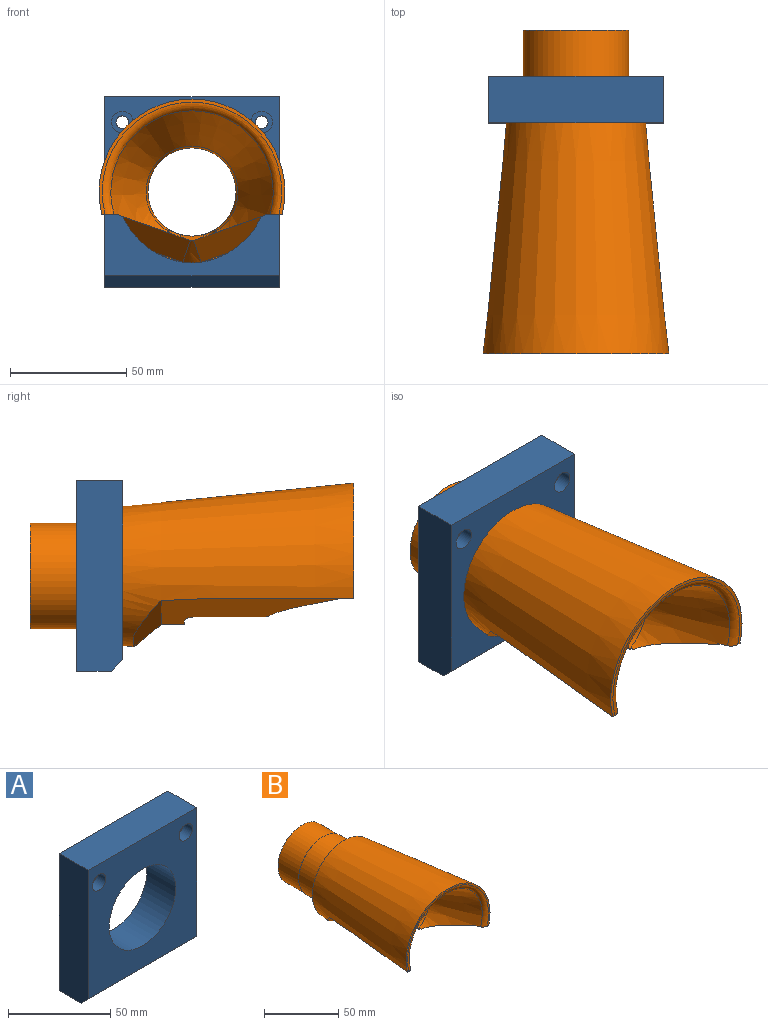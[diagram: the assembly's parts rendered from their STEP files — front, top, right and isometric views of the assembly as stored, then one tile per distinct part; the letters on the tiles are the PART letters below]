
ASSEMBLY  parts=2 mates=1
PART A: 14 faces, bbox 75x20x82 mm
  f0: plane 82x20mm, normal (1,0,0), area 1627.5mm2, adj f1,f3,f4,f5,f13
  f1: plane 75x20mm, normal (0,0,1), area 1500mm2, adj f0,f2,f4,f5
  f2: plane 82x20mm, normal (-1,0,0), area 1627.5mm2, adj f1,f3,f4,f5,f13
  f3: plane 75x15mm, normal (0,0,-1), area 1125mm2, adj f0,f2,f5,f13
  f4: plane 77x75mm, normal (0,-1,0), area 3974.3mm2, adj f0,f1,f2,f6,f9,f12,f13
  f5: plane 82x75mm, normal (0,1,0), area 4440.6mm2, adj f0,f1,f2,f3,f6,f7,f10
  f6: cylinder r=23mm len=46mm, axis (0,-1,0), area 2890.3mm2, adj f4,f5
  f7: cylinder r=2.75mm len=13.7mm, axis (0,-1,0), area 236.7mm2, adj f5,f8
  f8: plane 9.4x9.4mm, normal (0,-1,0), area 45.6mm2, adj f7,f9
  f9: cylinder r=4.7mm len=9.4mm, axis (0,-1,0), area 186mm2, adj f4,f8
  f10: cylinder r=2.75mm len=13.7mm, axis (0,-1,0), area 236.7mm2, adj f5,f11
  f11: plane 9.4x9.4mm, normal (0,-1,0), area 45.6mm2, adj f10,f12
  f12: cylinder r=4.7mm len=9.4mm, axis (0,-1,0), area 186mm2, adj f4,f11
  f13: plane 75x5mm, normal (0,-0.71,-0.71), area 530.3mm2, adj f0,f2,f3,f4
PART B: 30 faces, bbox 84.4x140.2x82.6 mm
  f0: plane 78.22x32.25mm, normal (0.33,0,-0.94), area 1465.1mm2, adj f2,f4,f12,f17,f20,f23,f24,f25
  f1: plane 78.22x32.25mm, normal (-0.33,0,-0.94), area 1465.1mm2, adj f2,f4,f12,f18,f22,f26,f27,f28
  f2: cylinder r=2mm len=10mm, axis (0,-1,0), area 13.6mm2, adj f0,f1,f21,f29
  f3: plane 10.77x3.81mm, normal (0,-1,0), area 4.1mm2, adj f4,f22
  f4: cone r=30mm half-angle=5.7deg, axis (0,-1,0), area 13541.2mm2, adj f0,f1,f3,f5,f11,f15,f16,f17
  f5: plane 80x49.62mm, normal (0,-1,0), area 193.6mm2, adj f4,f6,f16,f19
  f6: torus R=38.65mm, axis (0,-1,0), area 627.7mm2, adj f5,f12,f16,f19
  f7: plane 45.5x45.5mm, normal (0,1,0), area 491.9mm2, adj f8,f14
  f8: cylinder r=22.75mm len=45.5mm, axis (0,-1,0), area 2858.8mm2, adj f7,f9
  f9: plane 46x46mm, normal (0,1,0), area 35.9mm2, adj f8,f10
  f10: cylinder r=23mm len=46mm, axis (0,-1,0), area 2890.3mm2, adj f9,f11
  f11: plane 60x60mm, normal (0,1,0), area 1165.5mm2, adj f4,f10
  f12: cone r=19.8mm half-angle=23deg, axis (0,-1,0), area 4392.3mm2, adj f0,f1,f6,f13,f16,f17,f18,f19
  f13: torus R=29mm, axis (0,-1,0), area 402mm2, adj f12,f14,f23,f24,f26,f27
  f14: cylinder r=19mm len=97.46mm, axis (0,-1,0), area 11008.5mm2, adj f7,f13,f24,f25,f26,f28,f29
  f15: plane 10.77x3.81mm, normal (0,-1,0), area 4.1mm2, adj f4,f20
  f16: plane 57.63x6.13mm, normal (0,0,-1), area 167.1mm2, adj f4,f5,f6,f12,f17
  f17: cylinder r=2mm len=59.33mm, axis (0,-1,0), area 37.8mm2, adj f0,f4,f12,f16
  f18: cylinder r=2mm len=59.33mm, axis (0,-1,0), area 37.8mm2, adj f1,f4,f12,f19
  f19: plane 57.63x6.13mm, normal (0,0,-1), area 167.1mm2, adj f4,f5,f6,f12,f18
  f20: plane 29.17x19.65mm, normal (0.26,-0.64,-0.72), area 372.5mm2, adj f0,f4,f15,f21
  f21: bspline ~11.78x9.98mm, area 70.3mm2, adj f2,f4,f20,f22
  f22: bspline ~35.42x20.78mm, area 372.5mm2, adj f1,f3,f4,f21
  f23: plane 1.65x0.95mm, normal (-0.87,-0.5,0), area 0.5mm2, adj f0,f12,f13,f24
  f24: plane 29.81x1.43mm, normal (-1,0,0), area 41.5mm2, adj f0,f13,f14,f23,f25
  f25: cylinder r=5mm len=5mm, axis (0,0,-1), area 9.6mm2, adj f0,f14,f24,f29
  f26: plane 29.81x1.43mm, normal (1,0,0), area 41.5mm2, adj f1,f13,f14,f27,f28
  f27: plane 1.65x0.95mm, normal (0.87,-0.5,0), area 0.5mm2, adj f1,f12,f13,f26
  f28: cylinder r=5mm len=5mm, axis (0,0,-1), area 9.6mm2, adj f1,f14,f26,f29
  f29: plane 10x2.67mm, normal (0,-1,0), area 14.5mm2, adj f0,f1,f2,f14,f25,f28
PLACE A t=(0,20,53.62)mm
PLACE B t=(0,0,-11)mm
MATE fastened A.f6 <-> B.f6  axis (0,-1,0) through (0,0,53.62)mm
